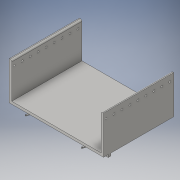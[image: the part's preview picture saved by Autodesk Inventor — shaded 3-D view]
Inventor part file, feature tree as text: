
AUTODESK INVENTOR PART (.ipt)
format: ipt  version: 2016 (Build 200138000, 138)  size: 220,160 bytes
history: native  units: in
note: dims shown in document units (in); Inventor stores cm internally (conversion verified against a paired STEP export)
features: sketch x11, hole x4, extrude x3, split x2, other x1, pattern_linear x1, fillet x1, sweep x1
ambient origin geometry x8: Origin, YZ Plane, XZ Plane, XY Plane, X Axis, Y Axis, Z Axis, Center Point
bodies: Solid1 (feature_tree)
feature tree (24):
  extrude  "Extrusion1"  Depth=0.125in
  sketch  "Sketch18"  dims[d88=0.0in d89=0.0in]
  extrude  "Extrusion3"  Depth=0.2in
  other  "Snap Fit1"
  sketch  "Sketch20"  dims[d97=3.8092in d98=0.5469in d99=7.6786in d100=4.1908in d101=0.0in d116=0.0in d117=4.2in d118=0.075in d121=1.0in d122=1.0in d123=0.1575in d124=0.75in d125=0.375in d126=0.25in d127=0.5635in d128=1.0in d129=0.8108in d130=1.0in d131=1.0in d132=0.1575in d133=0.75in d134=0.375in d135=0.25in d136=0.5635in d137=1.0in d138=0.8108in d139=1.0in d140=1.0in d141=0.1575in d142=0.75in d143=0.375in d144=0.25in d145=0.5635in d146=1.0in d147=0.8108in d174=5.0in d176=3.0in d177=3.0in d180=1.5in d184=7.4in d185=0.2in d186=0.2in d187=7.4in d188=0.0in d189=0.15in d190=0.08in d191=0.06in d192=0.04in d193=0.12in d194=0.08in d195=0.03in d196=0.03in d197=0.3436in d198=0.3436in d199=2.5in d201=1.0in d202=1.0in d203=0.1575in d204=0.75in d205=0.375in d206=0.25in d207=0.5635in d208=1.0in d209=0.8108in d210=3.5433in d212=0.625in d34=1.0in d35=1.0in d119=1.0in d120=1.0in]
  hole  "Hole7"  [1 undecoded]
  pattern_linear  "Rectangular Pattern2"  Spacing1=0.5469in  [1 undecoded]
  split  "Split1"
  extrude  "Extrusion2"  Depth=0.03in
  fillet  "Fillet1"  Radius=4.1908in
  sketch  "Sketch5"  dims[d80=4.0in]
  sweep  "Sweep1"
  split  "Split5"
  hole  "Hole2"  [1 undecoded]
  hole  "Hole3"  [1 undecoded]
  hole  "Hole4"  [1 undecoded]
  sketch  "Sketch17"  dims[d87=4.2in]
  sketch  "Sketch1"  dims[d0=7.4in d4=0.125in]
  sketch  "Sketch3"  dims[d6=0.075in d7=0.2in]
  sketch  "Sketch4"  dims[d9=0.125in d32=5.5in d33=0.0in]
  sketch  "Sketch6"  dims[d81=0.5in]
  sketch  "Sketch7"  dims[d84=2.8in d85=0.0in]
  sketch  "Sketch14"  dims[d86=0.125in]
  sketch  "Sketch19"  dims[d94=8.0in]
note: 5 required parameter values undecoded (feature->parameter linkage not recoverable at this tier; creation-order binding heuristic only, values carry confidence <= 0.55)
